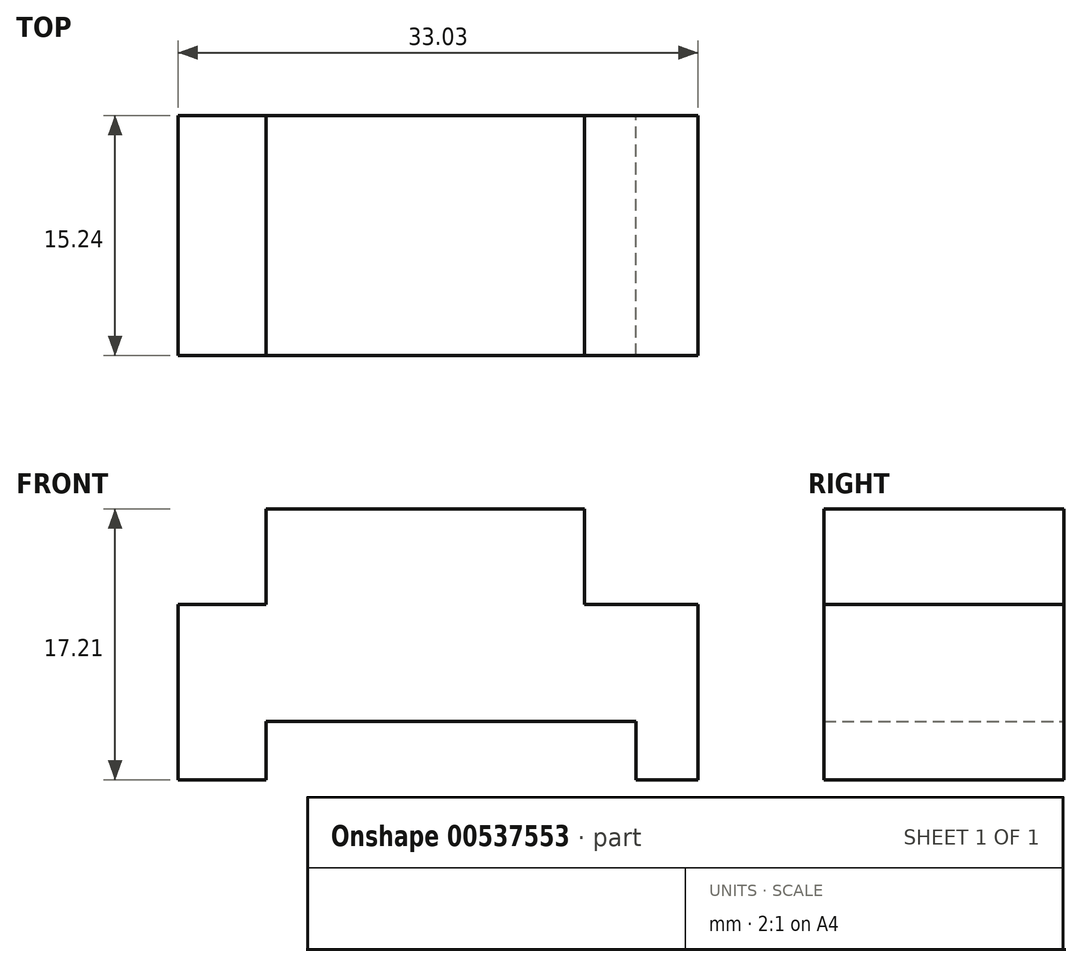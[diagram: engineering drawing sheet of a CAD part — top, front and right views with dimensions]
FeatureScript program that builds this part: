
annotation { "Feature Type Name" : "Feature", "Feature Type Description" : "" }
export const myFeature = defineFeature(function(context is Context, id is Id, definition is map)
    precondition{}
    {
        {
            var Q0;
            Q0=qCreatedBy(makeId("Front.planeOp"),FACE);
            var sketch = newSketch(context, id + "F0", { "sketchPlane" : qUnion([Q0])});
            skLineSegment(sketch, "E0", {"start": v(0, 0) * mm, "end": v(20.24, 0) * mm});
            skLineSegment(sketch, "E1", {"start": v(20.24, 0) * mm, "end": v(20.24, -6.05) * mm});
            skLineSegment(sketch, "E2", {"start": v(20.24, -6.05) * mm, "end": v(27.45, -6.05) * mm});
            skLineSegment(sketch, "E3", {"start": v(27.45, -6.05) * mm, "end": v(27.45, -17.21) * mm});
            skLineSegment(sketch, "E4", {"start": v(27.45, -17.21) * mm, "end": v(23.5, -17.21) * mm});
            skLineSegment(sketch, "E5", {"start": v(23.5, -17.21) * mm, "end": v(23.5, -13.5) * mm});
            skLineSegment(sketch, "E6", {"start": v(0, 0) * mm, "end": v(0, -6.05) * mm});
            skLineSegment(sketch, "E7", {"start": v(0, -6.05) * mm, "end": v(-5.58, -6.05) * mm});
            skLineSegment(sketch, "E8", {"start": v(-5.58, -6.05) * mm, "end": v(-5.58, -17.21) * mm});
            skLineSegment(sketch, "E9", {"start": v(-5.58, -17.21) * mm, "end": v(0, -17.21) * mm});
            skLineSegment(sketch, "E10", {"start": v(0, -17.21) * mm, "end": v(0, -13.5) * mm});
            skLineSegment(sketch, "E11", {"start": v(0, -13.5) * mm, "end": v(23.5, -13.5) * mm});
            skSolve(sketch);
        }
        {
            var Q0;
            Q0 = qSketchRegion(id + "F0", true);
            extrude(context, id + "F1", {"entities" : qUnion([Q0]), "depth" : 15.24 * mm, "offsetDistance" : 25.4 * mm});
        }
    });
